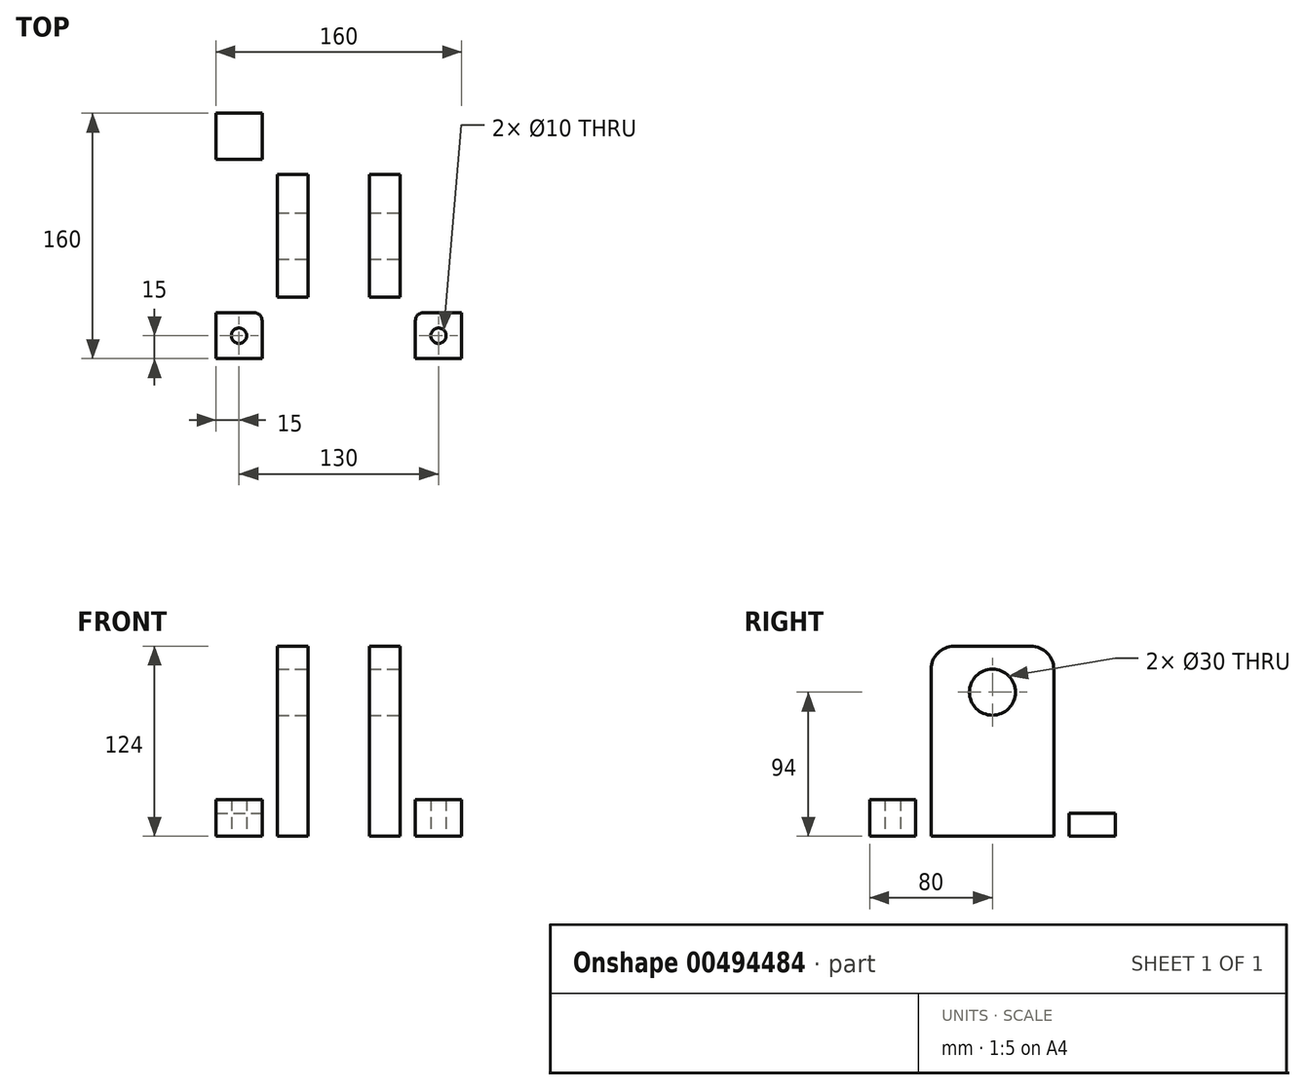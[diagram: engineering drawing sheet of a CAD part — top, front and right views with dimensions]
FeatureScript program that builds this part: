
annotation { "Feature Type Name" : "Feature", "Feature Type Description" : "" }
export const myFeature = defineFeature(function(context is Context, id is Id, definition is map)
    precondition{}
    {
        {
            var Q0;
            Q0=qCreatedBy(makeId("Top.planeOp"),FACE);
            var sketch = newSketch(context, id + "F0", { "sketchPlane" : qUnion([Q0])});
            skLineSegment(sketch, "E0.bottom", {"start": v(80, -80) * mm, "end": v(-80, -80) * mm});
            skLineSegment(sketch, "E0.top", {"start": v(80, 80) * mm, "end": v(-80, 80) * mm});
            skLineSegment(sketch, "E0.left", {"start": v(80, -80) * mm, "end": v(80, 80) * mm});
            skLineSegment(sketch, "E0.right", {"start": v(-80, -80) * mm, "end": v(-80, 80) * mm});
            skPoint(sketch, "E0.middle", {"position": v(0, 0) * mm});
            skLineSegment(sketch, "E1.bottom", {"start": v(-40, 40) * mm, "end": v(-20, 40) * mm});
            skLineSegment(sketch, "E1.top", {"start": v(-40, -40) * mm, "end": v(-20, -40) * mm});
            skLineSegment(sketch, "E1.left", {"start": v(-40, 40) * mm, "end": v(-40, -40) * mm});
            skLineSegment(sketch, "E1.right", {"start": v(-20, 40) * mm, "end": v(-20, -40) * mm});
            skLineSegment(sketch, "E2.bottom", {"start": v(20, 40) * mm, "end": v(40, 40) * mm});
            skLineSegment(sketch, "E2.top", {"start": v(20, -40) * mm, "end": v(40, -40) * mm});
            skLineSegment(sketch, "E2.left", {"start": v(20, 40) * mm, "end": v(20, -40) * mm});
            skLineSegment(sketch, "E2.right", {"start": v(40, 40) * mm, "end": v(40, -40) * mm});
            skLineSegment(sketch, "E3.bottom", {"start": v(50, 80) * mm, "end": v(80, 80) * mm});
            skLineSegment(sketch, "E3.top", {"start": v(50, 50) * mm, "end": v(80, 50) * mm});
            skLineSegment(sketch, "E3.left", {"start": v(50, 80) * mm, "end": v(50, 50) * mm});
            skLineSegment(sketch, "E3.right", {"start": v(80, 80) * mm, "end": v(80, 50) * mm});
            skLineSegment(sketch, "E4.bottom", {"start": v(-80, 50) * mm, "end": v(-50, 50) * mm});
            skLineSegment(sketch, "E4.top", {"start": v(-80, 80) * mm, "end": v(-50, 80) * mm});
            skLineSegment(sketch, "E4.left", {"start": v(-80, 50) * mm, "end": v(-80, 80) * mm});
            skLineSegment(sketch, "E4.right", {"start": v(-50, 50) * mm, "end": v(-50, 80) * mm});
            skLineSegment(sketch, "E5.bottom", {"start": v(-80, -50) * mm, "end": v(-50, -50) * mm});
            skLineSegment(sketch, "E5.top", {"start": v(-80, -80) * mm, "end": v(-50, -80) * mm});
            skLineSegment(sketch, "E5.left", {"start": v(-80, -50) * mm, "end": v(-80, -80) * mm});
            skLineSegment(sketch, "E5.right", {"start": v(-50, -50) * mm, "end": v(-50, -80) * mm});
            skLineSegment(sketch, "E6.bottom", {"start": v(50, -80) * mm, "end": v(80, -80) * mm});
            skLineSegment(sketch, "E6.top", {"start": v(50, -50) * mm, "end": v(80, -50) * mm});
            skLineSegment(sketch, "E6.left", {"start": v(50, -80) * mm, "end": v(50, -50) * mm});
            skLineSegment(sketch, "E6.right", {"start": v(80, -80) * mm, "end": v(80, -50) * mm});
            skPoint(sketch, "E7", {"position": v(-65, 65) * mm});
            skPoint(sketch, "E8", {"position": v(65, 65) * mm});
            skPoint(sketch, "E9", {"position": v(65, -65) * mm});
            skPoint(sketch, "E10", {"position": v(-65, -65) * mm});
            skPoint(sketch, "E10.positionSnap0", {"position": v(-50, -65) * mm});
            skSolve(sketch);
        }
        {
            var Q0;
            Q0=makeQuery(id+"F0.imprint","IMPRINT",FACE,{"disambiguationData":[TD([[makeQuery(id+"F0.imprint","IMPRINT",EDGE,{"derivedFrom":sQuery(id+"F0.wireOp",EDGE,"E0.bottom")}),-1.0]])]});
            extrude(context, id + "F1", {"entities" : qUnion([Q0]), "depth" : 24 * mm});
        }
        {
            var Q0;
            Q0=makeQuery(id+"F0.imprint","IMPRINT",FACE,{"disambiguationData":[TD([[makeQuery(id+"F0.imprint","IMPRINT",EDGE,{"derivedFrom":sQuery(id+"F0.wireOp",EDGE,"E5.bottom")}),-1.0]])]});
            var Q1;
            Q1=makeQuery(id+"F0.imprint","IMPRINT",FACE,{"disambiguationData":[TD([[makeQuery(id+"F0.imprint","IMPRINT",EDGE,{"derivedFrom":sQuery(id+"F0.wireOp",EDGE,"E6.bottom")}),1.0]])]});
            var Q2;
            Q2=makeQuery(id+"F0.imprint","IMPRINT",FACE,{"disambiguationData":[TD([[makeQuery(id+"F0.imprint","IMPRINT",EDGE,{"derivedFrom":sQuery(id+"F0.wireOp",EDGE,"E3.bottom")}),-1.0]])]});
            var Q3;
            Q3=makeQuery(id+"F0.imprint","IMPRINT",FACE,{"disambiguationData":[TD([[makeQuery(id+"F0.imprint","IMPRINT",EDGE,{"derivedFrom":sQuery(id+"F0.wireOp",EDGE,"E4.bottom")}),1.0]])]});
            extrude(context, id + "F2", {"entities" : qUnion([Q0, Q1, Q2, Q3]), "operationType" : NewBodyOperationType.ADD, "depth" : 15 * mm});
        }
        {
            var Q0;
            Q0=makeQuery(id+"F0.imprint","IMPRINT",FACE,{"disambiguationData":[TD([[makeQuery(id+"F0.imprint","IMPRINT",EDGE,{"derivedFrom":sQuery(id+"F0.wireOp",EDGE,"E1.bottom")}),-1.0]])]});
            var Q1;
            Q1=makeQuery(id+"F0.imprint","IMPRINT",FACE,{"disambiguationData":[TD([[makeQuery(id+"F0.imprint","IMPRINT",EDGE,{"derivedFrom":sQuery(id+"F0.wireOp",EDGE,"E2.bottom")}),-1.0]])]});
            extrude(context, id + "F3", {"entities" : qUnion([Q0, Q1]), "operationType" : NewBodyOperationType.ADD, "depth" : 124 * mm});
        }
        {
            var Q0;
            Q0=makeQuery(id+"F3.opExtrude","CAP_EDGE",EDGE,{"disambiguationData":[OSD([sQuery(id+"F0.wireOp",EDGE,"E1.top")])],"isStart":false});
            var Q1;
            Q1=makeQuery(id+"F3.opExtrude","CAP_EDGE",EDGE,{"disambiguationData":[OSD([sQuery(id+"F0.wireOp",EDGE,"E2.top")])],"isStart":false});
            var Q2;
            Q2=makeQuery(id+"F3.opExtrude","CAP_EDGE",EDGE,{"disambiguationData":[OSD([sQuery(id+"F0.wireOp",EDGE,"E2.bottom")])],"isStart":false});
            var Q3;
            Q3=makeQuery(id+"F3.opExtrude","CAP_EDGE",EDGE,{"disambiguationData":[OSD([sQuery(id+"F0.wireOp",EDGE,"E1.bottom")])],"isStart":false});
            var Q4;
            Q4=makeQuery(id+"F2.opExtrude","SWEPT_EDGE",EDGE,{"disambiguationData":[OSD([sQuery(id+"F0.wireOp",EDGE,"E5.top"),sQuery(id+"F0.wireOp",EDGE,"E5.left")])]});
            var Q5;
            Q5=makeQuery(id+"F2.opExtrude","SWEPT_EDGE",EDGE,{"disambiguationData":[OSD([sQuery(id+"F0.wireOp",EDGE,"E6.bottom"),sQuery(id+"F0.wireOp",EDGE,"E6.right")])]});
            var Q6;
            Q6=makeQuery(id+"F2.opExtrude","SWEPT_EDGE",EDGE,{"disambiguationData":[OSD([sQuery(id+"F0.wireOp",EDGE,"E4.top"),sQuery(id+"F0.wireOp",EDGE,"E4.left")])]});
            var Q7;
            Q7=makeQuery(id+"F2.opExtrude","SWEPT_EDGE",EDGE,{"disambiguationData":[OSD([sQuery(id+"F0.wireOp",EDGE,"E3.bottom"),sQuery(id+"F0.wireOp",EDGE,"E3.right")])]});
            fillet(context, id + "F4", {"entities" : qUnion([Q0, Q1, Q2, Q3, Q4, Q5, Q6, Q7]), "radius" : 15 * mm, "tangentPropagation" : true, "allowEdgeOverflow" : false});
        }
        {
            var Q0;
            Q0=makeQuery(id+"F1.opExtrude","SWEPT_EDGE",EDGE,{"disambiguationData":[OSD([sQuery(id+"F0.wireOp",EDGE,"E3.top"),sQuery(id+"F0.wireOp",EDGE,"E3.left")])]});
            var Q1;
            Q1=makeQuery(id+"F1.opExtrude","SWEPT_EDGE",EDGE,{"disambiguationData":[OSD([sQuery(id+"F0.wireOp",EDGE,"E4.bottom"),sQuery(id+"F0.wireOp",EDGE,"E4.right")])]});
            var Q2;
            Q2=makeQuery(id+"F1.opExtrude","SWEPT_EDGE",EDGE,{"disambiguationData":[OSD([sQuery(id+"F0.wireOp",EDGE,"E5.bottom"),sQuery(id+"F0.wireOp",EDGE,"E5.right")])]});
            var Q3;
            Q3=makeQuery(id+"F1.opExtrude","SWEPT_EDGE",EDGE,{"disambiguationData":[OSD([sQuery(id+"F0.wireOp",EDGE,"E6.top"),sQuery(id+"F0.wireOp",EDGE,"E6.left")])]});
            fillet(context, id + "F5", {"entities" : qUnion([Q0, Q1, Q2, Q3]), "radius" : 5 * mm, "tangentPropagation" : true, "allowEdgeOverflow" : false});
        }
        {
            var Q0;
            Q0=sQuery(id+"F0.wireOp",VERTEX,"E7");
            var Q1;
            Q1=sQuery(id+"F0.wireOp",VERTEX,"E10");
            var Q2;
            Q2=sQuery(id+"F0.wireOp",VERTEX,"E9");
            var Q3;
            Q3=sQuery(id+"F0.wireOp",VERTEX,"E8");
            var Q4;
            Q4=makeQuery(id+"F1.opExtrude","SWEPT_BODY",BODY,{"disambiguationData":[OSD([sQuery(id+"F0.wireOp",EDGE,"E0.bottom"),sQuery(id+"F0.wireOp",EDGE,"E0.top"),sQuery(id+"F0.wireOp",EDGE,"E0.left"),sQuery(id+"F0.wireOp",EDGE,"E0.right"),sQuery(id+"F0.wireOp",EDGE,"E1.bottom"),sQuery(id+"F0.wireOp",EDGE,"E1.top"),sQuery(id+"F0.wireOp",EDGE,"E1.left"),sQuery(id+"F0.wireOp",EDGE,"E1.right"),sQuery(id+"F0.wireOp",EDGE,"E2.bottom"),sQuery(id+"F0.wireOp",EDGE,"E2.top"),sQuery(id+"F0.wireOp",EDGE,"E2.left"),sQuery(id+"F0.wireOp",EDGE,"E2.right"),sQuery(id+"F0.wireOp",EDGE,"E3.top"),sQuery(id+"F0.wireOp",EDGE,"E3.left"),sQuery(id+"F0.wireOp",EDGE,"E4.bottom"),sQuery(id+"F0.wireOp",EDGE,"E4.right"),sQuery(id+"F0.wireOp",EDGE,"E5.bottom"),sQuery(id+"F0.wireOp",EDGE,"E5.right"),sQuery(id+"F0.wireOp",EDGE,"E6.top"),sQuery(id+"F0.wireOp",EDGE,"E6.left")])]});
            hole(context, id + "F6", {"style" : HoleStyle.SIMPLE, "endStyle" : HoleEndStyle.THROUGH, "oppositeDirection" : true, "holeDiameter" : 10 * mm, "isTappedThrough" : true, "tappedDepth" : 12 * mm, "tapClearance" : 3, "locations" : qUnion([Q0, Q1, Q2, Q3]), "scope" : qUnion([Q4])});
        }
        {
            var Q0;
            Q0=qCreatedBy(makeId("Right.planeOp"),FACE);
            var sketch = newSketch(context, id + "F7", { "sketchPlane" : qUnion([Q0])});
            skPoint(sketch, "E11", {"position": v(0, 94) * mm});
            skCircle(sketch, "E12", {"center": v(0, 94) * mm, "radius": 15 * mm});
            skSolve(sketch);
        }
        {
            var Q0;
            Q0=makeQuery(id+"F7.imprint","IMPRINT",FACE,{"disambiguationData":[TD([[makeQuery(id+"F7.imprint","IMPRINT",EDGE,{"derivedFrom":sQuery(id+"F7.wireOp",EDGE,"E12")}),1.0]])]});
            extrude(context, id + "F8", {"entities" : qUnion([Q0]), "operationType" : NewBodyOperationType.REMOVE, "endBound" : BoundingType.SYMMETRIC, "oppositeDirection" : true, "depth" : 104 * mm});
        }
    });
